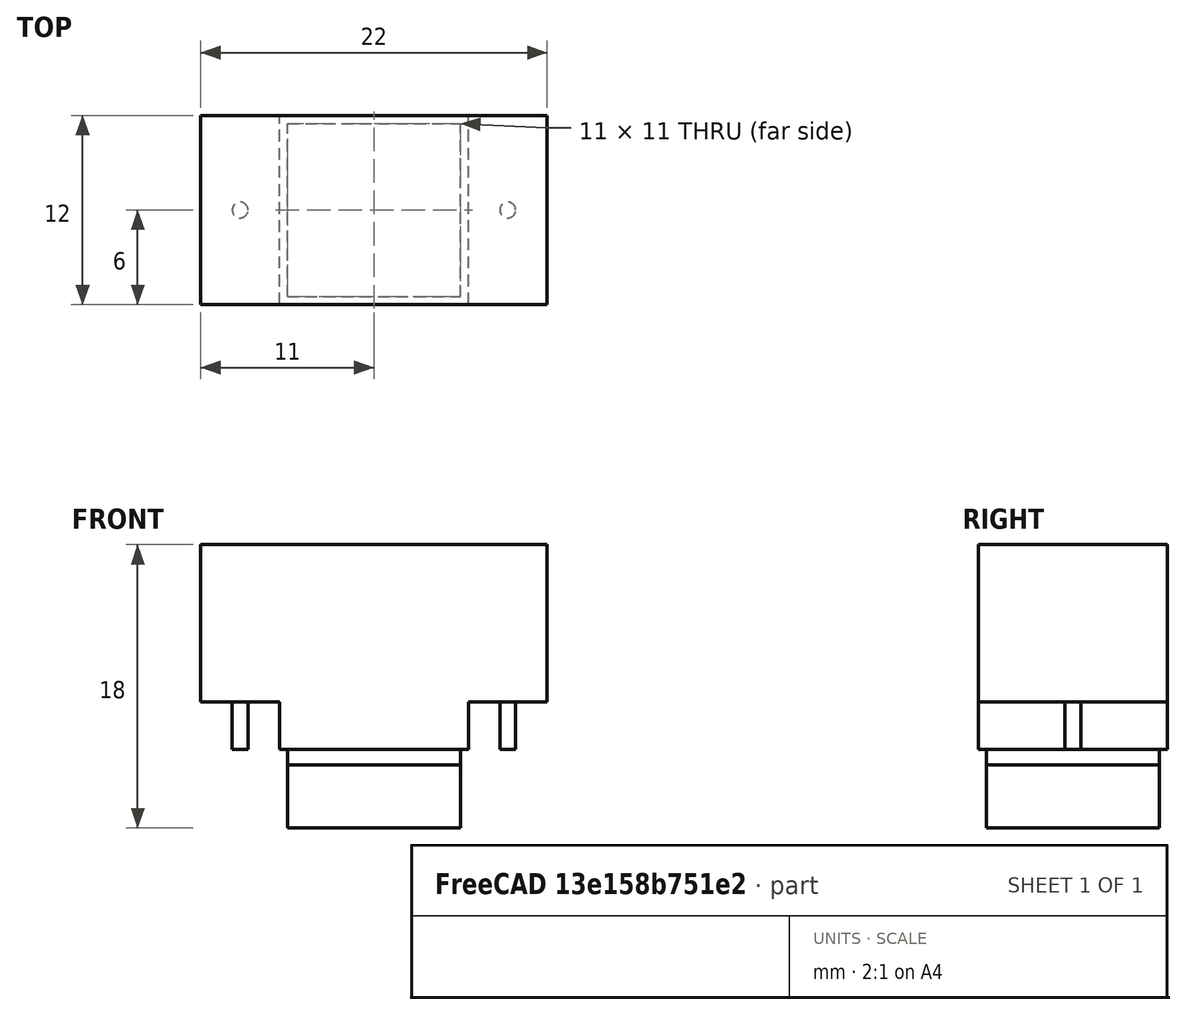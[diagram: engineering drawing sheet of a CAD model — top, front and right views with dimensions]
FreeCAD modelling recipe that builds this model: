
FCSTD DOCUMENT  (FreeCAD 0.17R13522 (Git))
Label: perforador_botones
License: CreativeCommons Attribution-ShareAlike
LicenseURL: http://creativecommons.org/licenses/by-sa/4.0/
objects: Part::Box×6, Part::Fuse×5, Part::Extrusion×2, Part::Cut×2, Part::Part2DObjectPython×1, Part::Feature×1
note: 17 computed .brp shape members not serialized (recipe doc carries the construction recipe); baked Part::Feature solids carry a one-line shape summary decoded from their .brp

FEATURE [Part::Box] Box  label="base principal"
  AttacherType = Attacher::AttachEngine3D
  Height = 10
  Length = 22
  Width = 12
FEATURE [Part::Box] Box001  label="posicion boton"
  AttacherType = Attacher::AttachEngine3D
  Height = 36
  Length = 22
  Placement = pos=(0,0,9) rot=(0,0,1;0rad)
  Width = 12
FEATURE [Part::Box] Box002  label="perforador 3 mm"
  AttacherType = Attacher::AttachEngine3D
  Height = 4
  Length = 12
  Placement = pos=(5,0,-3) rot=(0,0,1;0rad)
  Width = 12
FEATURE [Part::Box] Box003  label="perforador 1 mm"
  AttacherType = Attacher::AttachEngine3D
  Height = 1
  Length = 11
  Placement = pos=(5.5,0.5,-4) rot=(0,0,1;0rad)
  Width = 11
FEATURE [Part::Fuse] Fusion
  Base = -> Box002
  Refine = true
  Tool = -> Box003
FEATURE [Part::Part2DObjectPython] Circle  # Draft 2D object (typed FeaturePython)
  FirstAngle = 0
  LastAngle = 0
  MakeFace = true
  Placement = pos=(2.5,6,10) rot=(0,0,1;3.14159rad)
  Radius = 0.5
FEATURE [Part::Extrusion] Extrude  label="perforador tornillo izquierdo"
  Base = -> Circle
  Dir = (0,0,1)
  DirMode = 2
  FaceMakerClass = Part::FaceMakerBullseye
  LengthFwd = 40
  LengthRev = 0
  Placement = pos=(0,0,-13) rot=(0,0,1;0rad)
  Solid = false
  Symmetric = false
FEATURE [Part::Extrusion] Extrude001  label="perforador tornillo derecha"
  Base = -> Circle
  Dir = (0,0,1)
  DirMode = 2
  FaceMakerClass = Part::FaceMakerBullseye
  LengthFwd = 40
  LengthRev = 0
  Placement = pos=(17,0,-13) rot=(0,0,1;0rad)
  Solid = false
  Symmetric = false
FEATURE [Part::Cut] Cut
  Base = -> Extrude
  Refine = true
  Tool = -> Box001
FEATURE [Part::Box] Box004  label="Cube"
  AttacherType = Attacher::AttachEngine3D
  Height = 32
  Length = 10
  Placement = pos=(12,0,9) rot=(0,0,1;0rad)
  Width = 10
FEATURE [Part::Cut] Cut001
  Base = -> Extrude001
  Refine = true
  Tool = -> Box004
FEATURE [Part::Fuse] Fusion001
  Base = -> Box
  Refine = true
  Tool = -> Fusion
FEATURE [Part::Fuse] Fusion002
  Base = -> Cut
  Refine = true
  Tool = -> Fusion001
FEATURE [Part::Fuse] Fusion003  label="perforador"
  Base = -> Cut001
  Refine = true
  Tool = -> Fusion002
FEATURE [Part::Feature] Fusion003001  label="perforador001"
  shape: bbox 22 x 12 x 14 mm, 19 faces (baked)
FEATURE [Part::Box] Box005  label="Cube001"
  AttacherType = Attacher::AttachEngine3D
  Height = 5
  Length = 11
  Placement = pos=(5.5,0.5,-8) rot=(0,0,1;0rad)
  Width = 11
FEATURE [Part::Fuse] Fusion003002  label="el perforador"
  Base = -> Fusion003
  Refine = true
  Tool = -> Box005
